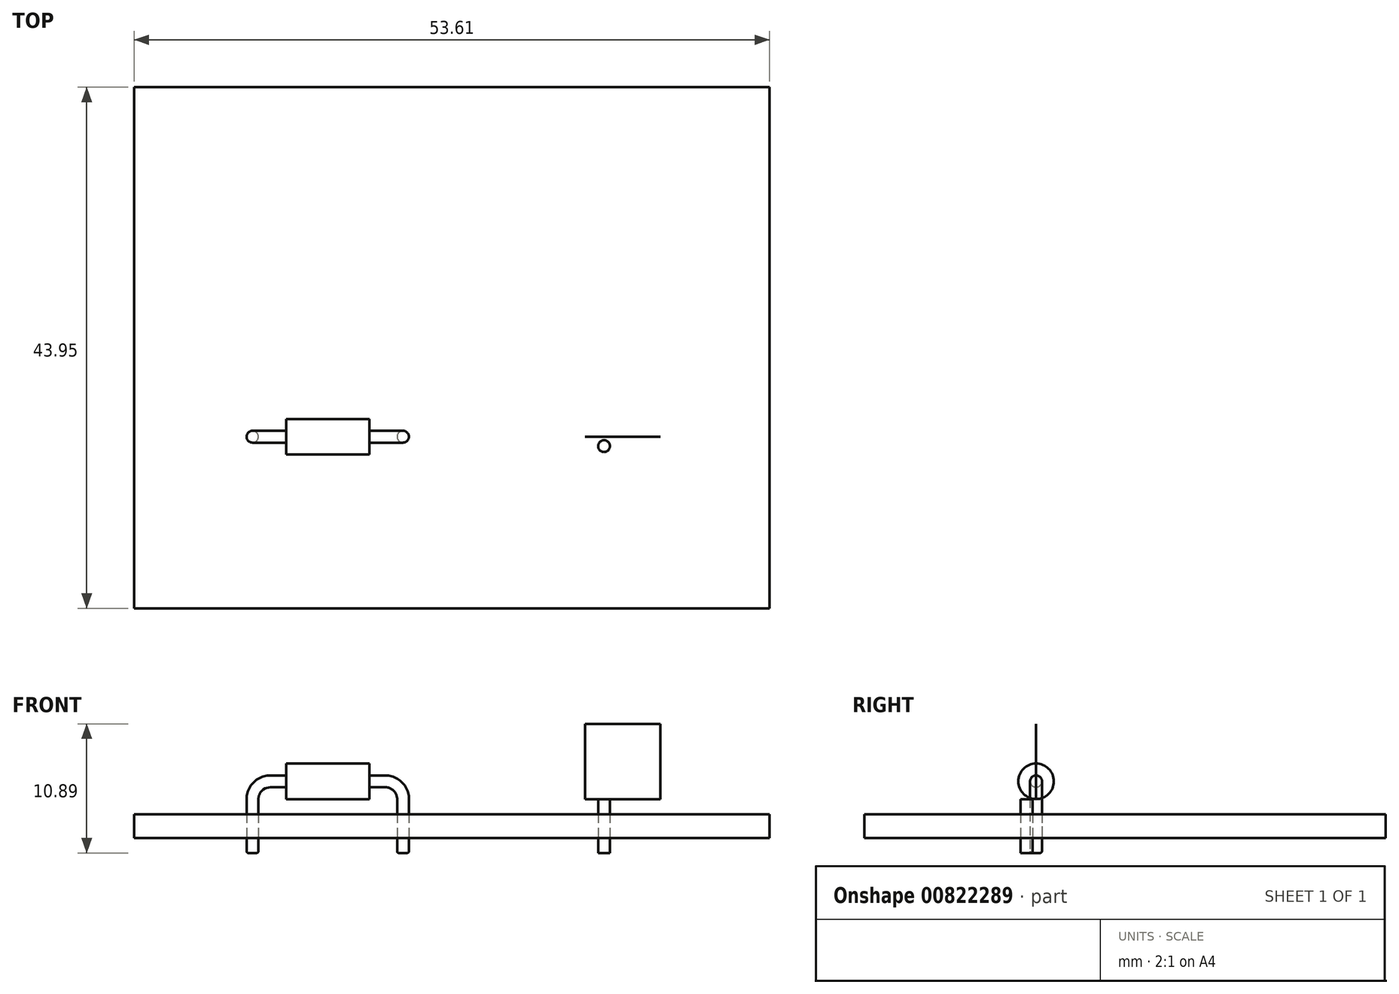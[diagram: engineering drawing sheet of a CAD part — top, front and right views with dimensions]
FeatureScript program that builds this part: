
annotation { "Feature Type Name" : "Feature", "Feature Type Description" : "" }
export const myFeature = defineFeature(function(context is Context, id is Id, definition is map)
    precondition{}
    {
        {
            var Q0;
            Q0=qCreatedBy(makeId("Top.planeOp"),FACE);
            var sketch = newSketch(context, id + "F0", { "sketchPlane" : qUnion([Q0])});
            skLineSegment(sketch, "E0.bottom", {"start": v(-30.42, -14.47) * mm, "end": v(23.19, -14.47) * mm});
            skLineSegment(sketch, "E0.top", {"start": v(-30.42, 29.48) * mm, "end": v(23.19, 29.48) * mm});
            skLineSegment(sketch, "E0.left", {"start": v(-30.42, -14.47) * mm, "end": v(-30.42, 29.48) * mm});
            skLineSegment(sketch, "E0.right", {"start": v(23.19, -14.47) * mm, "end": v(23.19, 29.48) * mm});
            skSolve(sketch);
        }
        {
            var Q0;
            Q0=makeQuery(id+"F0.imprint","IMPRINT",FACE,{"disambiguationData":[TD([[makeQuery(id+"F0.imprint","IMPRINT",EDGE,{"derivedFrom":sQuery(id+"F0.wireOp",EDGE,"E0.bottom")}),1.0]])]});
            extrude(context, id + "F1", {"entities" : qUnion([Q0]), "depth" : 2 * mm, "offsetDistance" : 25.4 * mm});
        }
        {
            var Q0;
            Q0=qCreatedBy(makeId("Front.planeOp"),FACE);
            var sketch = newSketch(context, id + "F2", { "sketchPlane" : qUnion([Q0])});
            skLineSegment(sketch, "E1.bottom", {"start": v(-17.58, 4.77) * mm, "end": v(-10.58, 4.77) * mm});
            skLineSegment(sketch, "E1.top", {"start": v(-17.58, 6.27) * mm, "end": v(-10.58, 6.27) * mm});
            skLineSegment(sketch, "E1.left", {"start": v(-17.58, 4.77) * mm, "end": v(-17.58, 6.27) * mm});
            skLineSegment(sketch, "E1.right", {"start": v(-10.58, 4.77) * mm, "end": v(-10.58, 6.27) * mm});
            skPoint(sketch, "E2", {"position": v(-14.08, 6.27) * mm});
            skLineSegment(sketch, "E3", {"start": v(-14.08, 10.24) * mm, "end": v(-14.08, 0.38) * mm, "construction": true});
            skPoint(sketch, "E3.endSnap0", {"position": v(-14.08, 4.77) * mm});
            skLineSegment(sketch, "E4.MirrorCS", {"start": v(-17.58, 3.27) * mm, "end": v(-10.58, 3.27) * mm, "construction": true});
            skLineSegment(sketch, "E5.MirrorCS", {"start": v(-17.58, 4.77) * mm, "end": v(-17.58, 3.27) * mm, "construction": true});
            skLineSegment(sketch, "E6.MirrorCS", {"start": v(-10.58, 4.77) * mm, "end": v(-10.58, 3.27) * mm, "construction": true});
            skSolve(sketch);
        }
        {
            var Q0;
            Q0=makeQuery(id+"F2.imprint","IMPRINT",FACE,{"disambiguationData":[TD([[makeQuery(id+"F2.imprint","IMPRINT",EDGE,{"derivedFrom":sQuery(id+"F2.wireOp",EDGE,"E1.bottom")}),1.0]])]});
            var Q1;
            Q1=sQuery(id+"F2.wireOp",EDGE,"E1.bottom");
            revolve(context, id + "F3", {"surfaceOperationType" : NewSurfaceOperationType.NEW, "entities" : qUnion([Q0]), "axis" : qUnion([Q1]), "revolveType" : RevolveType.FULL});
        }
        {
            var Q0;
            Q0=makeQuery(id+"F3.opRevolve","SWEPT_FACE",FACE,{"disambiguationData":[OSD([sQuery(id+"F2.wireOp",EDGE,"E1.left")])]});
            var sketch = newSketch(context, id + "F4", { "sketchPlane" : qUnion([Q0])});
            skCircle(sketch, "E7", {"center": v(0, 4.77) * mm, "radius": 0.5 * mm});
            skSolve(sketch);
        }
        {
            var Q0;
            Q0=qCreatedBy(makeId("Front.planeOp"),FACE);
            var sketch = newSketch(context, id + "F5", { "sketchPlane" : qUnion([Q0])});
            skPoint(sketch, "E8.0", {"position": v(-17.58, 4.77) * mm});
            skLineSegment(sketch, "E9", {"start": v(-17.58, 4.77) * mm, "end": v(-18.93, 4.77) * mm});
            skLineSegment(sketch, "E10", {"start": v(-20.43, 3.27) * mm, "end": v(-20.43, -1.27) * mm});
            skPoint(sketch, "E11.visualSharp", {"position": v(-20.43, 4.77) * mm});
            skArc(sketch, "E11.filletArc", {"start": v(-18.93, 4.77) * mm, "mid": v(-20, 4.33) * mm, "end": v(-20.43, 3.27) * mm});
            skSolve(sketch);
        }
        {
            var Q0;
            Q0=makeQuery(id+"F4.imprint","IMPRINT",FACE,{"disambiguationData":[TD([[makeQuery(id+"F4.imprint","IMPRINT",EDGE,{"derivedFrom":sQuery(id+"F4.wireOp",EDGE,"E7")}),1.0]])]});
            var Q1;
            Q1 = qConstructionFilter(qBodyType(qCreatedBy(id + "F5" ,EDGE), BodyType.WIRE), ConstructionObject.NO);
            sweep(context, id + "F6", {"profiles" : qUnion([Q0]), "path" : qUnion([Q1])});
        }
        {
            var Q0;
            Q0=makeQuery(id+"F6.opSweep","CAP_EDGE",EDGE,{"disambiguationData":[OSD([sQuery(id+"F4.wireOp",EDGE,"E7"),sQuery(id+"F5.wireOp",VERTEX,"E10.end")])],"isStart":false});
            fillet(context, id + "F7", {"entities" : qUnion([Q0]), "radius" : .15 * mm, "tangentPropagation" : true, "allowEdgeOverflow" : false});
        }
        {
            var Q0;
            Q0=sQuery(id+"F2.wireOp",EDGE,"E3");
            cPlane(context, id + "F8", {"entities" : qUnion([Q0]), "cplaneType" : CPlaneType.LINE_ANGLE, "offset" : 25.4 * mm, "angle" : 0 * degree, "width" : 152.4 * mm, "height" : 152.4 * mm});
        }
        {
            var Q0;
            Q0=makeQuery(id+"F6.opSweep","SWEPT_BODY",BODY,{"disambiguationData":[OSD([sQuery(id+"F4.wireOp",EDGE,"E7"),sQuery(id+"F5.wireOp",EDGE,"E10")])]});
            var Q1;
            Q1=qCreatedBy(id+"F8.planeOp",FACE);
            mirror(context, id + "F9", {"entities" : qUnion([Q0]), "mirrorPlane" : qUnion([Q1])});
        }
        {
            var Q0;
            Q0=qCreatedBy(makeId("Front.planeOp"),FACE);
            var sketch = newSketch(context, id + "F10", { "sketchPlane" : qUnion([Q0])});
            skLineSegment(sketch, "E12.bottom", {"start": v(7.63, 3.27) * mm, "end": v(13.98, 3.27) * mm});
            skLineSegment(sketch, "E12.top", {"start": v(7.63, 9.62) * mm, "end": v(13.98, 9.62) * mm});
            skLineSegment(sketch, "E12.left", {"start": v(7.63, 3.27) * mm, "end": v(7.63, 9.62) * mm});
            skLineSegment(sketch, "E12.right", {"start": v(13.98, 3.27) * mm, "end": v(13.98, 9.62) * mm});
            skSolve(sketch);
        }
        {
            var Q0;
            Q0=makeQuery(id+"F10.imprint","IMPRINT",FACE,{"disambiguationData":[TD([[makeQuery(id+"F10.imprint","IMPRINT",EDGE,{"derivedFrom":sQuery(id+"F10.wireOp",EDGE,"E12.bottom")}),1.0]])]});
            extrude(context, id + "F11", {"entities" : qUnion([Q0]), "depth" : 1 / 406.4 * mm, "offsetDistance" : 25.4 * mm});
        }
        {
            var Q0;
            Q0=makeQuery(id+"F11.opExtrude","SWEPT_FACE",FACE,{"disambiguationData":[OSD([sQuery(id+"F10.wireOp",EDGE,"E12.bottom")])]});
            var sketch = newSketch(context, id + "F12", { "sketchPlane" : qUnion([Q0])});
            skLineSegment(sketch, "E13.0", {"start": v(13.98, 1.59) * mm, "end": v(13.98, 0) * mm, "construction": true});
            skLineSegment(sketch, "E13.1", {"start": v(7.63, 1.59) * mm, "end": v(13.98, 1.59) * mm, "construction": true});
            skLineSegment(sketch, "E13.2", {"start": v(7.63, 0) * mm, "end": v(13.98, 0) * mm, "construction": true});
            skLineSegment(sketch, "E13.3", {"start": v(7.63, 1.59) * mm, "end": v(7.63, 0) * mm, "construction": true});
            skLineSegment(sketch, "E14", {"start": v(10.8, 1.59) * mm, "end": v(10.8, 0) * mm, "construction": true});
            skCircle(sketch, "E15", {"center": v(9.22, 0.8) * mm, "radius": 0.5 * mm});
            skPoint(sketch, "E15.centerSnap0", {"position": v(10.8, 0.8) * mm});
            skCircle(sketch, "E16.MirrorC", {"center": v(12.4, 0.8) * mm, "radius": 0.5 * mm});
            skSolve(sketch);
        }
        {
            var Q0;
            Q0=qCreatedBy(makeId("Front.planeOp"),FACE);
            var sketch = newSketch(context, id + "F13", { "sketchPlane" : qUnion([Q0])});
            skPoint(sketch, "E17.0", {"position": v(9.22, 3.27) * mm});
            skPoint(sketch, "E18.0", {"position": v(12.4, 3.27) * mm});
            skLineSegment(sketch, "E19", {"start": v(9.22, 3.27) * mm, "end": v(9.22, -1.27) * mm});
            skLineSegment(sketch, "E20", {"start": v(12.4, 3.27) * mm, "end": v(12.4, -1.27) * mm});
            skSolve(sketch);
        }
        {
            var Q0;
            Q0=makeQuery(id+"F12.imprint","IMPRINT",FACE,{"disambiguationData":[TD([[makeQuery(id+"F12.imprint","IMPRINT",EDGE,{"derivedFrom":sQuery(id+"F12.wireOp",EDGE,"E15")}),1.0]])]});
            var Q1;
            Q1=makeQuery(id+"F12.imprint","IMPRINT",FACE,{"disambiguationData":[TD([[makeQuery(id+"F12.imprint","IMPRINT",EDGE,{"derivedFrom":sQuery(id+"F12.wireOp",EDGE,"E16.MirrorC")}),-1.0]])]});
            var Q2;
            Q2=sQuery(id+"F13.wireOp",EDGE,"E19");
            sweep(context, id + "F14", {"profiles" : qUnion([Q0, Q1]), "path" : qUnion([Q2])});
        }
    });
